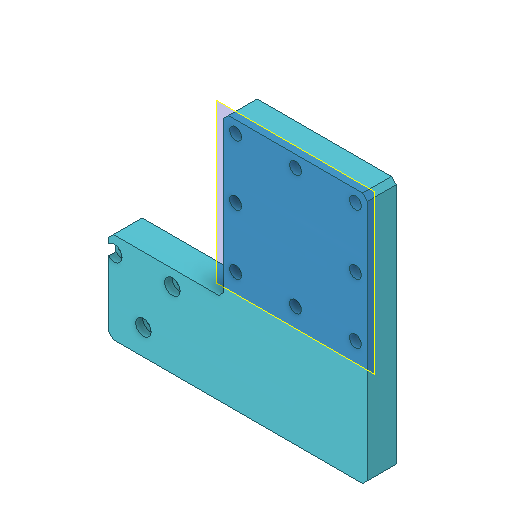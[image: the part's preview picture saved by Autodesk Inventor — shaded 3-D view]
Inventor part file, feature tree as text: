
AUTODESK INVENTOR PART (.ipt)
format: ipt  version: 2022 (Build 260153000, 153)  size: 194,048 bytes
history: native  units: mm
features: other x7, reference x5, sketch x3, hole x2, plane x1, extrude x1, chamfer x1, projected_geometry x1
ambient origin geometry x8: Origin, YZ Plane, XZ Plane, XY Plane, X Axis, Y Axis, Z Axis, Center Point
bodies: Body1 (feature_tree)
feature tree (21):
  plane  "Arbeitsebene2"
  extrude  "Extrusion1"  Depth=30.0mm
  chamfer  "Fase1"  Distance=45.0mm
  hole  "Bohrung2"  [1 undecoded]
  hole  "Bohrung3"  [1 undecoded]
  sketch  "Skizze6"  dims[d10=30.0mm d11=30.0mm]
  reference  "Referenz1"
  reference  "Referenz2"
  sketch  "Skizze7"  dims[d12=30.0mm]
  projected_geometry  "Projizierte Kontur2"
  sketch  "Skizze8"  dims[d13=30.0mm d14=45.0mm d15=18.0mm d16=12.0mm d17=0.0mm d18=2.0mm d19=2.0mm d20=45.0deg d21=5.0mm d22=6.0mm d23=8.0mm d24=5.0mm d25=90.0deg d26=8.0mm d27=20.594885mm d28=8.0mm d29=2.8mm d30=6.0mm d31=6.5mm d32=3.0mm d33=90.0deg d34=8.0mm d35=20.594885mm]
  reference  "Referenz3"
  reference  "Referenz4"
  reference  "Referenz5"
  other  "<userpath>\Documents\GitHub\cellstorm\INVENTOR\cellSTORM_v6.iam"
  other  "cellSTORM_v6.iam"
  other  "00_XY_stage-CHUO_SEIKI_LD-647-R1:1"
  other  "00_XY_stage-CHUO_SEIKI_LD-647-R1-Bottom:1"
  other  "cellSTORM_v5_microsocpe:1"
  other  "30_Cube_Z_Focus_MGN12_NEMA_slide_part2:1"
  other  "cellSTORM_v5_chiptray_old_0:1"
note: 2 required parameter values undecoded (feature->parameter linkage not recoverable at this tier; creation-order binding heuristic only, values carry confidence <= 0.55)
